FCSTD DOCUMENT  (FreeCAD 0.20R29177 (Git))
Label: Mount Template 110mm
License: All rights reserved
LicenseURL: http://en.wikipedia.org/wiki/All_rights_reserved
objects: Sketcher::SketchObject×2, PartDesign::Body×1
note: 3 computed .brp shape members not serialized (recipe doc carries the construction recipe); baked Part::Feature solids carry a one-line shape summary decoded from their .brp

FEATURE [Sketcher::SketchObject] Sketch002
  FullyConstrained = false
  MapMode = 2
  sketch-geometry (26):
    g0: LineSegment StartX=65.06 StartY=-23 StartZ=0 EndX=65.06 EndY=-14.75 EndZ=0
    g1: LineSegment StartX=64.94 StartY=23 StartZ=0 EndX=-65.06 EndY=23 EndZ=0
    g2: LineSegment StartX=-65.06 StartY=23 StartZ=0 EndX=-65.06 EndY=-23 EndZ=0
    g3: LineSegment StartX=-65.06 StartY=-23 StartZ=0 EndX=65.06 EndY=-23 EndZ=0
    g4: GeomPoint X=0 Y=0 Z=0
    g5: ArcOfCircle CenterX=-57.06 CenterY=16.95 CenterZ=0 NormalX=0 NormalY=0 NormalZ=1 AngleXU=0 Radius=2.05 StartAngle=1.5708 EndAngle=4.71239
    g6: ArcOfCircle CenterX=-53.06 CenterY=16.95 CenterZ=0 NormalX=0 NormalY=0 NormalZ=1 AngleXU=0 Radius=2.05 StartAngle=4.71239 EndAngle=7.85398
    g7: LineSegment StartX=-57.06 StartY=14.9 StartZ=0 EndX=-53.06 EndY=14.9 EndZ=0
    g8: LineSegment StartX=-53.06 StartY=19 StartZ=0 EndX=-57.06 EndY=19 EndZ=0
    g9: ArcOfCircle CenterX=-57.06 CenterY=-16.9634 CenterZ=0 NormalX=0 NormalY=0 NormalZ=1 AngleXU=0 Radius=2.05 StartAngle=1.5708 EndAngle=4.71239
    g10: ArcOfCircle CenterX=-53.06 CenterY=-16.9634 CenterZ=0 NormalX=0 NormalY=0 NormalZ=1 AngleXU=0 Radius=2.05 StartAngle=4.71239 EndAngle=7.85398
    g11: LineSegment StartX=-57.06 StartY=-14.9134 StartZ=0 EndX=-53.06 EndY=-14.9134 EndZ=0
    g12: LineSegment StartX=-53.06 StartY=-19.0134 StartZ=0 EndX=-57.06 EndY=-19.0134 EndZ=0
    g13: ArcOfCircle CenterX=57.06 CenterY=-16.9782 CenterZ=0 NormalX=0 NormalY=0 NormalZ=1 AngleXU=0 Radius=2.05 StartAngle=4.71239 EndAngle=7.85398
    g14: ArcOfCircle CenterX=53.06 CenterY=-16.9782 CenterZ=0 NormalX=0 NormalY=0 NormalZ=1 AngleXU=0 Radius=2.05 StartAngle=1.5708 EndAngle=4.71239
    g15: LineSegment StartX=57.06 StartY=-14.9282 StartZ=0 EndX=53.06 EndY=-14.9282 EndZ=0
    g16: LineSegment StartX=53.06 StartY=-19.0282 StartZ=0 EndX=57.06 EndY=-19.0282 EndZ=0
    g17: ArcOfCircle CenterX=56.94 CenterY=16.9561 CenterZ=0 NormalX=0 NormalY=0 NormalZ=1 AngleXU=0 Radius=2.05 StartAngle=4.71239 EndAngle=7.85398
    g18: ArcOfCircle CenterX=52.94 CenterY=16.9561 CenterZ=0 NormalX=0 NormalY=0 NormalZ=1 AngleXU=0 Radius=2.05 StartAngle=1.5708 EndAngle=4.71239
    g19: LineSegment StartX=56.94 StartY=14.9061 StartZ=0 EndX=52.94 EndY=14.9061 EndZ=0
    g20: LineSegment StartX=52.94 StartY=19.0061 StartZ=0 EndX=56.94 EndY=19.0061 EndZ=0
    g21: LineSegment StartX=64.94 StartY=14.75 StartZ=0 EndX=-10.06 EndY=14.75 EndZ=0
    g22: LineSegment StartX=-10.06 StartY=14.75 StartZ=0 EndX=-10.06 EndY=-14.75 EndZ=0
    g23: LineSegment StartX=-10.06 StartY=-14.75 StartZ=0 EndX=65.06 EndY=-14.75 EndZ=0
    g24: GeomPoint X=27.5 Y=0 Z=0
    g25: LineSegment StartX=64.94 StartY=14.75 StartZ=0 EndX=64.94 EndY=23 EndZ=0
  constraints (63):
    c: Coincident(g25,g1)
    c: Coincident(g1,g2)
    c: Coincident(g2,g3)
    c: Coincident(g3,g0)
    c: Horizontal(g1)
    c: Horizontal(g3)
    c: Vertical(g0)
    c: Vertical(g2)
    c: Symmetric(g1,g0,g4)
    c: Coincident(g4,g-1)
    c: DistanceX(g1,g1) = 130
    c: DistanceY(g0,g25) = 46
    c: Tangent(g5,g7) = -1.5708
    c: Tangent(g7,g6) = -1.5708
    c: Tangent(g6,g8) = -1.5708
    c: Tangent(g8,g5) = -1.5708
    c: Equal(g5,g6)
    c: DistanceX(g8,g8) = 4
    c: Distance(g5,g2) = 8
    c: Radius(g6) = 2.05
    c: Horizontal(g8)
    c: Distance(g6,g1) = 4
    c: Tangent(g9,g11) = 1.5708
    c: Tangent(g11,g10) = 1.5708
    c: Tangent(g10,g12) = 1.5708
    c: Tangent(g12,g9) = 1.5708
    c: Equal(g9,g10)
    c: Radius(g10) = 2.05
    c: Horizontal(g12)
    c: Tangent(g13,g15) = -1.5708
    c: Tangent(g15,g14) = -1.5708
    c: Tangent(g14,g16) = -1.5708
    c: Tangent(g16,g13) = -1.5708
    c: Equal(g13,g14)
    c: Radius(g14) = 2.05
    c: Horizontal(g16)
    c: Tangent(g17,g19) = 1.5708
    c: Tangent(g19,g18) = 1.5708
    c: Tangent(g18,g20) = 1.5708
    c: Tangent(g20,g17) = 1.5708
    c: Equal(g17,g18)
    c: Radius(g18) = 2.05
    c: Horizontal(g20)
    c: Coincident(g21,g22)
    c: Coincident(g22,g23)
    c: Horizontal(g21)
    c: Horizontal(g23)
    c: Vertical(g22)
    c: Symmetric(g21,g23,g24)
    c: PointOnObject(g24,g-1)
    c: DistanceY(g22,g22) = 29.5
    c: DistanceX(g2,g9) = 8
    c: Vertical(g25)
    c: DistanceX(g11,g11) = 4
    c: DistanceX(g16,g16) = 4
    c: DistanceX(g2,g4) = 65.06
    c: DistanceX(g17,g1) = 8
    c: DistanceX(g20,g20) = 4
    c: DistanceX(g13,g0) = 8
    c: PointOnObject(g21,g25)
    c: DistanceY(g25,g25) = 8.25
    c: DistanceX(g21,g21) = 75
    c: Coincident(g23,g0)
FEATURE [Sketcher::SketchObject] Sketch003
  ExternalGeometry = -> [Sketch002]
  FullyConstrained = false
  MapMode = 5
  Placement = pos=(0,0,10) rot=(0,0,1;0rad)
  sketch-geometry (16):
    g0: ArcOfCircle CenterX=-57.06 CenterY=16.95 CenterZ=0 NormalX=0 NormalY=0 NormalZ=1 AngleXU=0 Radius=4 StartAngle=1.5708 EndAngle=4.71239
    g1: ArcOfCircle CenterX=-53.06 CenterY=16.95 CenterZ=0 NormalX=0 NormalY=0 NormalZ=1 AngleXU=0 Radius=4 StartAngle=4.71239 EndAngle=7.85398
    g2: LineSegment StartX=-57.06 StartY=12.95 StartZ=0 EndX=-53.06 EndY=12.95 EndZ=0
    g3: LineSegment StartX=-53.06 StartY=20.95 StartZ=0 EndX=-57.06 EndY=20.95 EndZ=0
    g4: ArcOfCircle CenterX=-57.06 CenterY=-16.95 CenterZ=0 NormalX=0 NormalY=0 NormalZ=1 AngleXU=0 Radius=4 StartAngle=1.5708 EndAngle=4.71239
    g5: ArcOfCircle CenterX=-53.06 CenterY=-16.95 CenterZ=0 NormalX=0 NormalY=0 NormalZ=1 AngleXU=0 Radius=4 StartAngle=4.71239 EndAngle=7.85398
    g6: LineSegment StartX=-57.06 StartY=-12.95 StartZ=0 EndX=-53.06 EndY=-12.95 EndZ=0
    g7: LineSegment StartX=-53.06 StartY=-20.95 StartZ=0 EndX=-57.06 EndY=-20.95 EndZ=0
    g8: ArcOfCircle CenterX=57.06 CenterY=16.95 CenterZ=0 NormalX=0 NormalY=0 NormalZ=1 AngleXU=0 Radius=4 StartAngle=4.71239 EndAngle=7.85398
    g9: ArcOfCircle CenterX=53.06 CenterY=16.95 CenterZ=0 NormalX=0 NormalY=0 NormalZ=1 AngleXU=0 Radius=4 StartAngle=1.5708 EndAngle=4.71239
    g10: LineSegment StartX=57.06 StartY=12.95 StartZ=0 EndX=53.06 EndY=12.95 EndZ=0
    g11: LineSegment StartX=53.06 StartY=20.95 StartZ=0 EndX=57.06 EndY=20.95 EndZ=0
    g12: ArcOfCircle CenterX=57.06 CenterY=-16.95 CenterZ=0 NormalX=0 NormalY=0 NormalZ=1 AngleXU=0 Radius=4 StartAngle=4.71239 EndAngle=7.85398
    g13: ArcOfCircle CenterX=53.06 CenterY=-16.95 CenterZ=0 NormalX=0 NormalY=0 NormalZ=1 AngleXU=0 Radius=4 StartAngle=1.5708 EndAngle=4.71239
    g14: LineSegment StartX=57.06 StartY=-12.95 StartZ=0 EndX=53.06 EndY=-12.95 EndZ=0
    g15: LineSegment StartX=53.06 StartY=-20.95 StartZ=0 EndX=57.06 EndY=-20.95 EndZ=0
  constraints (26):
    c: Tangent(g0,g2) = -1.5708
    c: Tangent(g2,g1) = -1.5708
    c: Tangent(g1,g3) = -1.5708
    c: Tangent(g3,g0) = -1.5708
    c: Equal(g0,g1)
    c: Coincident(g0,g-4)
    c: Coincident(g1,g-5)
    c: Radius(g1) = 4
    c: Tangent(g4,g6) = 1.5708
    c: Tangent(g6,g5) = 1.5708
    c: Tangent(g5,g7) = 1.5708
    c: Tangent(g7,g4) = 1.5708
    c: Equal(g4,g5)
    c: Radius(g5) = 4
    c: Tangent(g8,g10) = 1.5708
    c: Tangent(g10,g9) = 1.5708
    c: Tangent(g9,g11) = 1.5708
    c: Tangent(g11,g8) = 1.5708
    c: Equal(g8,g9)
    c: Radius(g9) = 4
    c: Tangent(g12,g14) = -1.5708
    c: Tangent(g14,g13) = -1.5708
    c: Tangent(g13,g15) = -1.5708
    c: Tangent(g15,g12) = -1.5708
    c: Equal(g12,g13)
    c: Radius(g13) = 4
FEATURE [PartDesign::Body] Body001  label="Body"
  Group = -> [Sketch002,Sketch003]
  Origin = -> Origin003
